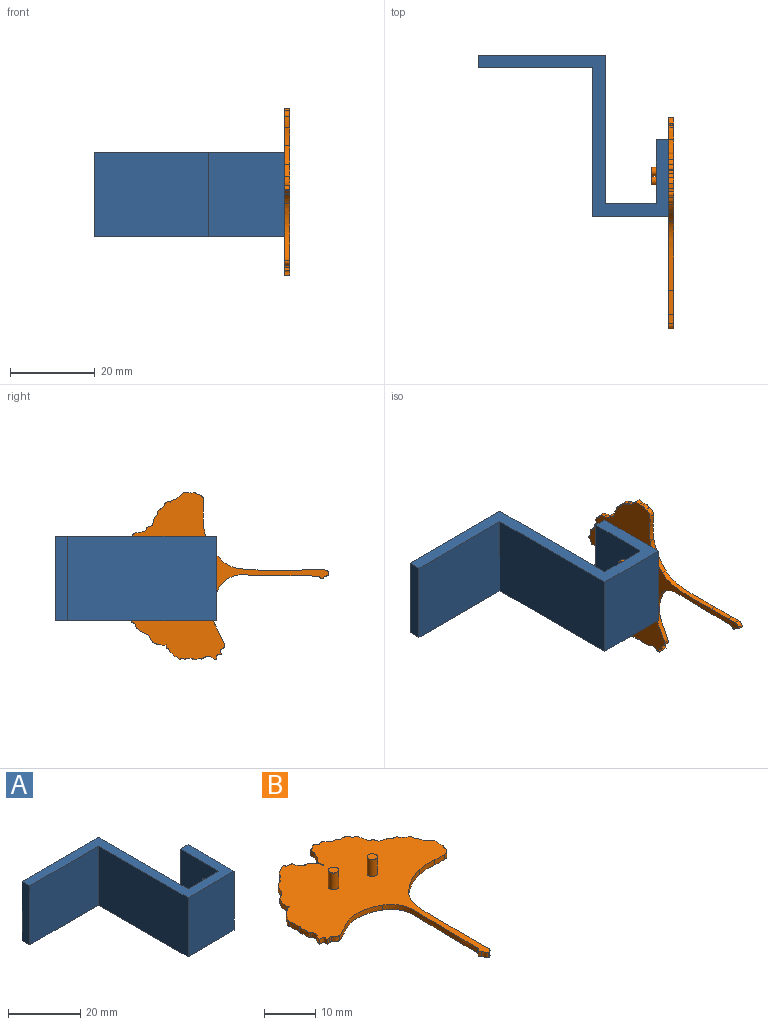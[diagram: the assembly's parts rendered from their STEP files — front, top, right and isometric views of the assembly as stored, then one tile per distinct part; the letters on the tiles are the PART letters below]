
ASSEMBLY  parts=2 mates=1
PART A: 14 faces, bbox 45x38x20 mm
  f0: plane 20x3mm, normal (0,1,0), area 60mm2, adj f1,f9,f10,f11
  f1: plane 20x15mm, normal (-1,0,0), area 293.7mm2, adj f0,f2,f10,f11,f12,f13
  f2: plane 20x12mm, normal (0,1,0), area 240mm2, adj f1,f3,f10,f11
  f3: plane 35x20mm, normal (1,0,0), area 700mm2, adj f2,f4,f10,f11
  f4: plane 30x20mm, normal (0,1,0), area 600mm2, adj f3,f5,f10,f11
  f5: plane 20x3mm, normal (-1,0,0), area 60mm2, adj f4,f6,f10,f11
  f6: plane 27x20mm, normal (0,-1,0), area 540mm2, adj f5,f7,f10,f11
  f7: plane 35x20mm, normal (-1,0,0), area 700mm2, adj f6,f8,f10,f11
  f8: plane 20x18mm, normal (0,-1,0), area 360mm2, adj f7,f9,f10,f11
  f9: plane 20x18mm, normal (1,0,0), area 353.7mm2, adj f0,f8,f10,f11,f12,f13
  f10: plane 45x38mm, normal (0,0,1), area 285mm2, adj f0,f1,f2,f3,f4,f5,f6,f7
  f11: plane 45x38mm, normal (0,0,-1), area 285mm2, adj f0,f1,f2,f3,f4,f5,f6,f7
  f12: cylinder r=1mm len=3mm, axis (1,0,0), area 18.8mm2, adj f1,f9
  f13: cylinder r=1mm len=3mm, axis (1,0,0), area 18.8mm2, adj f1,f9
PART B: 57 faces, bbox 39.6x50x5.2 mm
  f0: extruded ~1.2x0.15mm, area 0.2mm2, adj f1,f50,f51,f52
  f1: extruded ~1.2x0.13mm, area 0.2mm2, adj f0,f2,f51,f52
  f2: extruded ~1.2x0.91mm, area 1.5mm2, adj f1,f3,f51,f52
  f3: extruded ~1.76x1.39mm, area 3.6mm2, adj f2,f4,f51,f52
  f4: extruded ~3.12x1.81mm, area 5mm2, adj f3,f5,f51,f52
  f5: extruded ~8.87x6.44mm, area 14mm2, adj f4,f6,f51,f52
  f6: extruded ~3.52x3.46mm, area 6.8mm2, adj f5,f7,f51,f52
  f7: plane 1.2x0.12mm, normal (0.46,-0.89,0), area 0.2mm2, adj f6,f8,f51,f52
  f8: extruded ~2.95x1.2mm, area 3.6mm2, adj f7,f9,f51,f52
  f9: plane 1.2x0.28mm, normal (0.37,0.93,0), area 0.4mm2, adj f8,f10,f51,f52
  f10: extruded ~2.64x1.2mm, area 3.3mm2, adj f9,f11,f51,f52
  f11: extruded ~3.01x1.2mm, area 4mm2, adj f10,f12,f51,f52
  f12: extruded ~1.2x1.17mm, area 2.5mm2, adj f11,f13,f51,f52
  f13: extruded ~1.2x0.74mm, area 0.9mm2, adj f12,f14,f51,f52
  f14: extruded ~1.2x0.47mm, area 0.6mm2, adj f13,f15,f51,f52
  f15: extruded ~1.23x1.2mm, area 1.9mm2, adj f14,f16,f51,f52
  f16: extruded ~13.36x2.85mm, area 17mm2, adj f15,f17,f51,f52
  f17: extruded ~23.31x3.11mm, area 29.3mm2, adj f16,f18,f51,f52
  f18: extruded ~1.2x0.58mm, area 0.8mm2, adj f17,f19,f51,f52
  f19: extruded ~1.2x0.85mm, area 1.3mm2, adj f18,f20,f51,f52
  f20: extruded ~1.23x1.2mm, area 1.7mm2, adj f19,f21,f51,f52
  f21: plane 1.2x0.3mm, normal (0,-1,0), area 0.4mm2, adj f20,f22,f51,f52
  f22: extruded ~1.2x1.2mm, area 1.9mm2, adj f21,f23,f51,f52
  f23: extruded ~2.22x1.2mm, area 2.7mm2, adj f22,f24,f51,f52
  f24: extruded ~5.67x1.2mm, area 6.8mm2, adj f23,f25,f51,f52
  f25: extruded ~16.27x2.36mm, area 20.1mm2, adj f24,f26,f51,f52
  f26: extruded ~2.76x2.23mm, area 4.3mm2, adj f25,f27,f51,f52
  f27: extruded ~4.39x1.87mm, area 5.8mm2, adj f26,f28,f51,f52
  f28: extruded ~4.24x1.2mm, area 5.1mm2, adj f27,f29,f51,f52
  f29: extruded ~2.77x1.2mm, area 3.3mm2, adj f28,f30,f51,f52
  f30: extruded ~1.36x1.33mm, area 2.5mm2, adj f29,f31,f51,f52
  f31: extruded ~1.58x1.2mm, area 2.1mm2, adj f30,f32,f51,f52
  f32: extruded ~1.2x0.59mm, area 0.7mm2, adj f31,f33,f51,f52
  f33: extruded ~1.27x1.2mm, area 1.5mm2, adj f32,f34,f51,f52
  f34: plane 1.2x0.19mm, normal (-0.36,0.93,0), area 0.3mm2, adj f33,f35,f51,f52
  f35: extruded ~1.38x1.2mm, area 2.1mm2, adj f34,f36,f51,f52
  f36: extruded ~1.2x1.13mm, area 1.5mm2, adj f35,f37,f51,f52
  f37: extruded ~1.2x0.57mm, area 1mm2, adj f36,f38,f51,f52
  f38: extruded ~1.2x0.2mm, area 0.2mm2, adj f37,f39,f51,f52
  f39: extruded ~1.24x1.2mm, area 1.8mm2, adj f38,f40,f51,f52
  f40: extruded ~1.23x1.2mm, area 2.1mm2, adj f39,f41,f51,f52
  f41: extruded ~4.65x3.18mm, area 7.2mm2, adj f40,f42,f51,f52
  f42: extruded ~1.61x1.2mm, area 2.3mm2, adj f41,f43,f51,f52
  f43: extruded ~3.99x3.19mm, area 7.5mm2, adj f42,f44,f51,f52
  f44: extruded ~1.55x1.2mm, area 2.1mm2, adj f43,f45,f51,f52
  f45: extruded ~4.57x1.99mm, area 8.1mm2, adj f44,f46,f51,f52
  f46: extruded ~2.93x1.93mm, area 4.4mm2, adj f45,f47,f51,f52
  f47: extruded ~1.35x1.2mm, area 1.7mm2, adj f46,f48,f51,f52
  f48: extruded ~1.2x0.98mm, area 1.2mm2, adj f47,f49,f51,f52
  f49: extruded ~2.21x1.71mm, area 3.4mm2, adj f48,f50,f51,f52
  f50: plane 1.2x0.1mm, normal (-0.96,0.29,0), area 0.1mm2, adj f0,f49,f51,f52
  f51: plane 49.96x39.57mm, normal (0,0,1), area 706.6mm2, adj f0,f1,f2,f3,f4,f5,f6,f7
  f52: plane 49.96x39.57mm, normal (0,0,-1), area 712.9mm2, adj f0,f1,f2,f3,f4,f5,f6,f7
  f53: cylinder r=1mm len=4mm, axis (0,0,-1), area 25.1mm2, adj f51,f54
  f54: plane 2x2mm, normal (0,0,1), area 3.1mm2, adj f53
  f55: cylinder r=1mm len=4mm, axis (0,0,-1), area 25.1mm2, adj f51,f56
  f56: plane 2x2mm, normal (0,0,1), area 3.1mm2, adj f55
PLACE A t=(-24.38,-32.2,-6.69)mm
PLACE B rot(axis=(0,-1,0),90deg) t=(-6.38,-1.23,4.46)mm
MATE fastened B.f55 <-> A.f12  axis (1,0,0) through (-9.38,-26.86,7.15)mm
